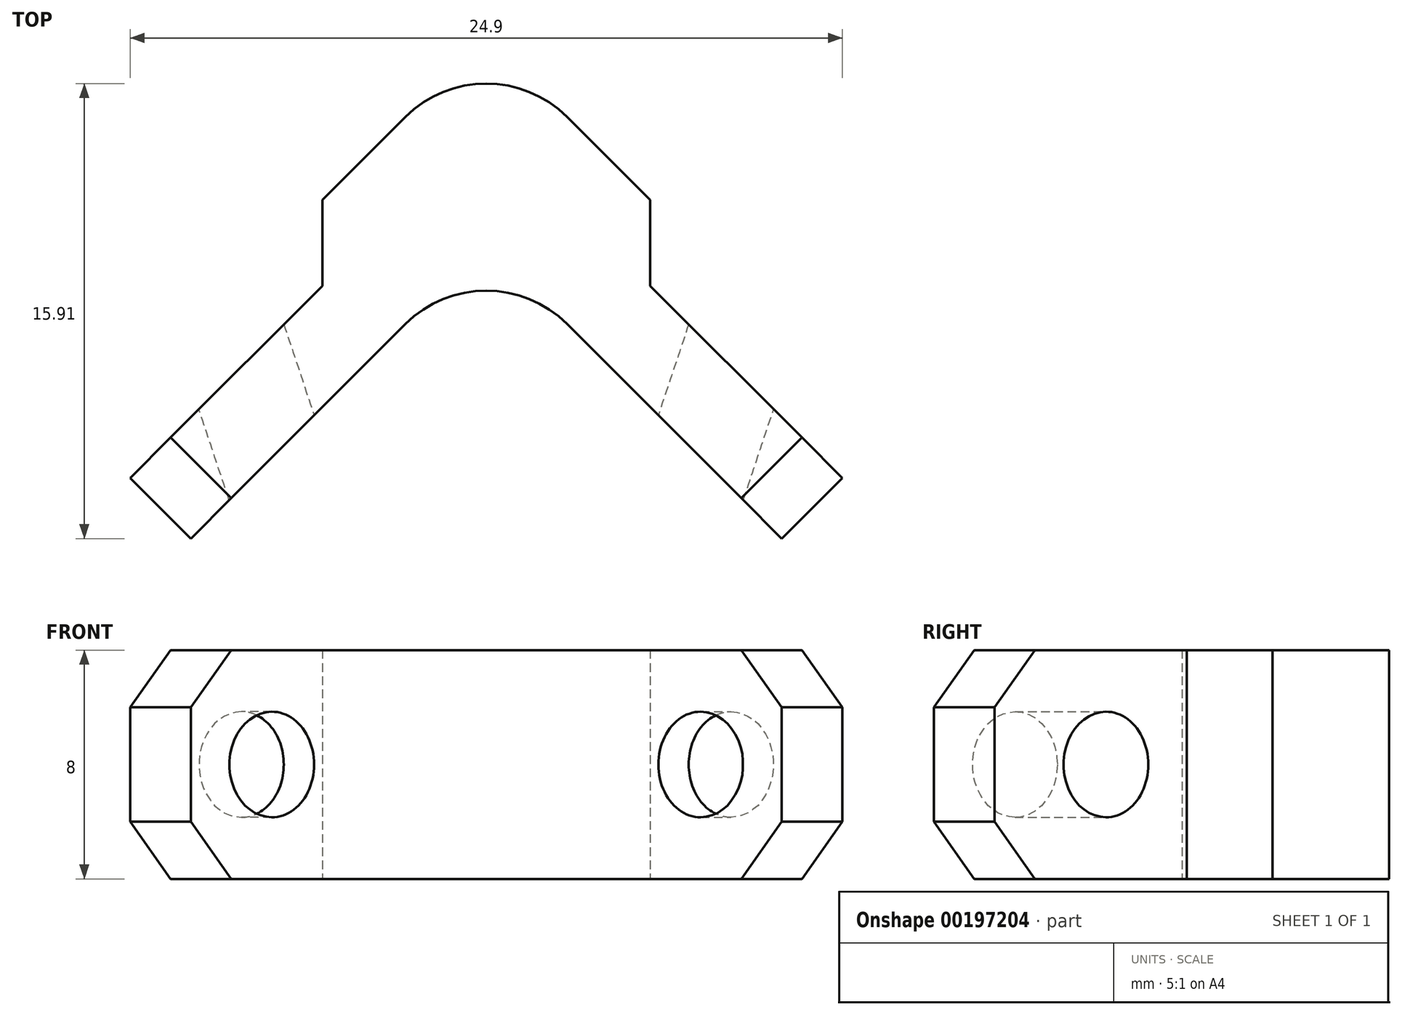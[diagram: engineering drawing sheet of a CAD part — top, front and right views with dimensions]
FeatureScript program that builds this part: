
annotation { "Feature Type Name" : "Feature", "Feature Type Description" : "" }
export const myFeature = defineFeature(function(context is Context, id is Id, definition is map)
    precondition{}
    {
        {
            var Q0;
            Q0=qCreatedBy(makeId("Top.planeOp"),FACE);
            var sketch = newSketch(context, id + "F0", { "sketchPlane" : qUnion([Q0])});
            skLineSegment(sketch, "E0", {"start": v(0, 0) * mm, "end": v(12.45, -12.45) * mm});
            skLineSegment(sketch, "E1", {"start": v(12.45, -12.45) * mm, "end": v(10.33, -14.57) * mm});
            skLineSegment(sketch, "E2", {"start": v(10.33, -14.57) * mm, "end": v(0, -4.24) * mm});
            skLineSegment(sketch, "E3", {"start": v(0, 0) * mm, "end": v(0, -4.24) * mm, "construction": true});
            skLineSegment(sketch, "E4.MirrorCS", {"start": v(0, 0) * mm, "end": v(-12.45, -12.45) * mm});
            skLineSegment(sketch, "E5.MirrorCS", {"start": v(-10.33, -14.57) * mm, "end": v(0, -4.24) * mm});
            skLineSegment(sketch, "E6.MirrorCS", {"start": v(-12.45, -12.45) * mm, "end": v(-10.33, -14.57) * mm});
            skPoint(sketch, "E7", {"position": v(7.5, -11.74) * mm});
            skPoint(sketch, "E8", {"position": v(-7.5, -11.74) * mm});
            skLineSegment(sketch, "E9", {"start": v(5.73, -5.73) * mm, "end": v(5.73, -2.73) * mm});
            skLineSegment(sketch, "E10", {"start": v(5.73, -2.73) * mm, "end": v(0, 3) * mm});
            skLineSegment(sketch, "E11.MirrorCS", {"start": v(-5.73, -2.73) * mm, "end": v(0, 3) * mm});
            skLineSegment(sketch, "E12.MirrorCS", {"start": v(-5.73, -5.73) * mm, "end": v(-5.73, -2.73) * mm});
            skLineSegment(sketch, "E13", {"start": v(7.5, -11.74) * mm, "end": v(13.86, -5.38) * mm, "construction": true});
            skSolve(sketch);
        }
        {
            var Q0;
            Q0=makeQuery(id+"F0.imprint","IMPRINT",FACE,{"disambiguationData":[TD([[makeQuery(id+"F0.imprint","IMPRINT",EDGE,{"derivedFrom":sQuery(id+"F0.wireOp",EDGE,"E0")}),-1.0]])]});
            var Q1;
            {var subQ0=sQuery(id+"F0.wireOp",EDGE,"E9");Q1=makeQuery(id+"F0.imprint","IMPRINT",FACE,{"disambiguationData":[TD([[makeQuery(id+"F0.imprint","IMPRINT",EDGE,{"derivedFrom":subQ0}),1.0]])]});}
            extrude(context, id + "F1", {"entities" : qUnion([Q0, Q1]), "depth" : 8 * mm});
        }
        {
            var Q0;
            Q0=makeQuery(id+"F1.opExtrude","SWEPT_FACE",FACE,{"disambiguationData":[OSD([sQuery(id+"F0.wireOp",EDGE,"E2")])]});
            var sketch = newSketch(context, id + "F2", { "sketchPlane" : qUnion([Q0])});
            skEllipse(sketch, "E14", {"center": v(13.6, 4) * mm, "majorRadius": 2.1 * mm, "minorRadius": 1.85 * mm, "majorAxis": v(-1, 0)});
            skSolve(sketch);
        }
        {
            var Q0;
            Q0=makeQuery(id+"F1.opExtrude","SWEPT_FACE",FACE,{"disambiguationData":[OSD([sQuery(id+"F0.wireOp",EDGE,"E0")])]});
            var sketch = newSketch(context, id + "F3", { "sketchPlane" : qUnion([Q0])});
            skEllipse(sketch, "E15", {"center": v(-12.1, 4) * mm, "majorRadius": 2.1 * mm, "minorRadius": 1.85 * mm, "majorAxis": v(1, 0)});
            skSolve(sketch);
        }
        {
            var Q1;
            Q1=makeQuery(id+"F3.imprint","IMPRINT",FACE,{"disambiguationData":[TD([[makeQuery(id+"F3.imprint","IMPRINT",EDGE,{"derivedFrom":sQuery(id+"F3.wireOp",EDGE,"E15")}),1.0]])]});
            var Q2;
            Q2=makeQuery(id+"F2.imprint","IMPRINT",FACE,{"disambiguationData":[TD([[makeQuery(id+"F2.imprint","IMPRINT",EDGE,{"derivedFrom":sQuery(id+"F2.wireOp",EDGE,"E14")}),1.0]])]});
            loft(context, id + "F4", {"operationType" : NewBodyOperationType.REMOVE, "sheetProfilesArray" : [{ "sheetProfileEntities" : qUnion([Q1]) }, { "sheetProfileEntities" : qUnion([Q2]) }]});
        }
        {
            var Q0;
            Q0=makeQuery(id+"F4.boolean.opBoolean","COPY",FACE,{"derivedFrom":makeQuery(id+"F4.opLoft","SWEPT_FACE",FACE,{"disambiguationData":[OSD([sQuery(id+"F2.wireOp",EDGE,"E14"),sQuery(id+"F3.wireOp",EDGE,"E15")])]})});
            var Q1;
            Q1=qCreatedBy(makeId("Right.planeOp"),FACE);
            mirror(context, id + "F5", {"patternType" : MirrorType.FACE, "faces" : qUnion([Q0]), "mirrorPlane" : qUnion([Q1])});
        }
        {
            var Q0;
            Q0=makeQuery(id+"F1.opExtrude","SWEPT_EDGE",EDGE,{"disambiguationData":[OSD([sQuery(id+"F0.wireOp",EDGE,"E2"),sQuery(id+"F0.wireOp",EDGE,"E5.MirrorCS")])]});
            var Q1;
            Q1=makeQuery(id+"F1.opExtrude","SWEPT_EDGE",EDGE,{"disambiguationData":[OSD([sQuery(id+"F0.wireOp",EDGE,"E10"),sQuery(id+"F0.wireOp",EDGE,"E11.MirrorCS")])]});
            fillet(context, id + "F6", {"entities" : qUnion([Q0, Q1]), "radius" : 4 * mm, "tangentPropagation" : true, "allowEdgeOverflow" : false});
        }
        {
            var Q0;
            Q0=makeQuery(id+"F1.opExtrude","CAP_EDGE",EDGE,{"disambiguationData":[OSD([sQuery(id+"F0.wireOp",EDGE,"E1")])],"isStart":false});
            var Q1;
            Q1=makeQuery(id+"F1.opExtrude","CAP_EDGE",EDGE,{"disambiguationData":[OSD([sQuery(id+"F0.wireOp",EDGE,"E1")])],"isStart":true});
            var Q2;
            Q2=makeQuery(id+"F1.opExtrude","CAP_EDGE",EDGE,{"disambiguationData":[OSD([sQuery(id+"F0.wireOp",EDGE,"E6.MirrorCS")])],"isStart":false});
            var Q3;
            Q3=makeQuery(id+"F1.opExtrude","CAP_EDGE",EDGE,{"disambiguationData":[OSD([sQuery(id+"F0.wireOp",EDGE,"E6.MirrorCS")])],"isStart":true});
            chamfer(context, id + "F7", {"entities" : qUnion([Q0, Q1, Q2, Q3]), "width" : 2 * mm, "tangentPropagation" : true});
        }
    });
